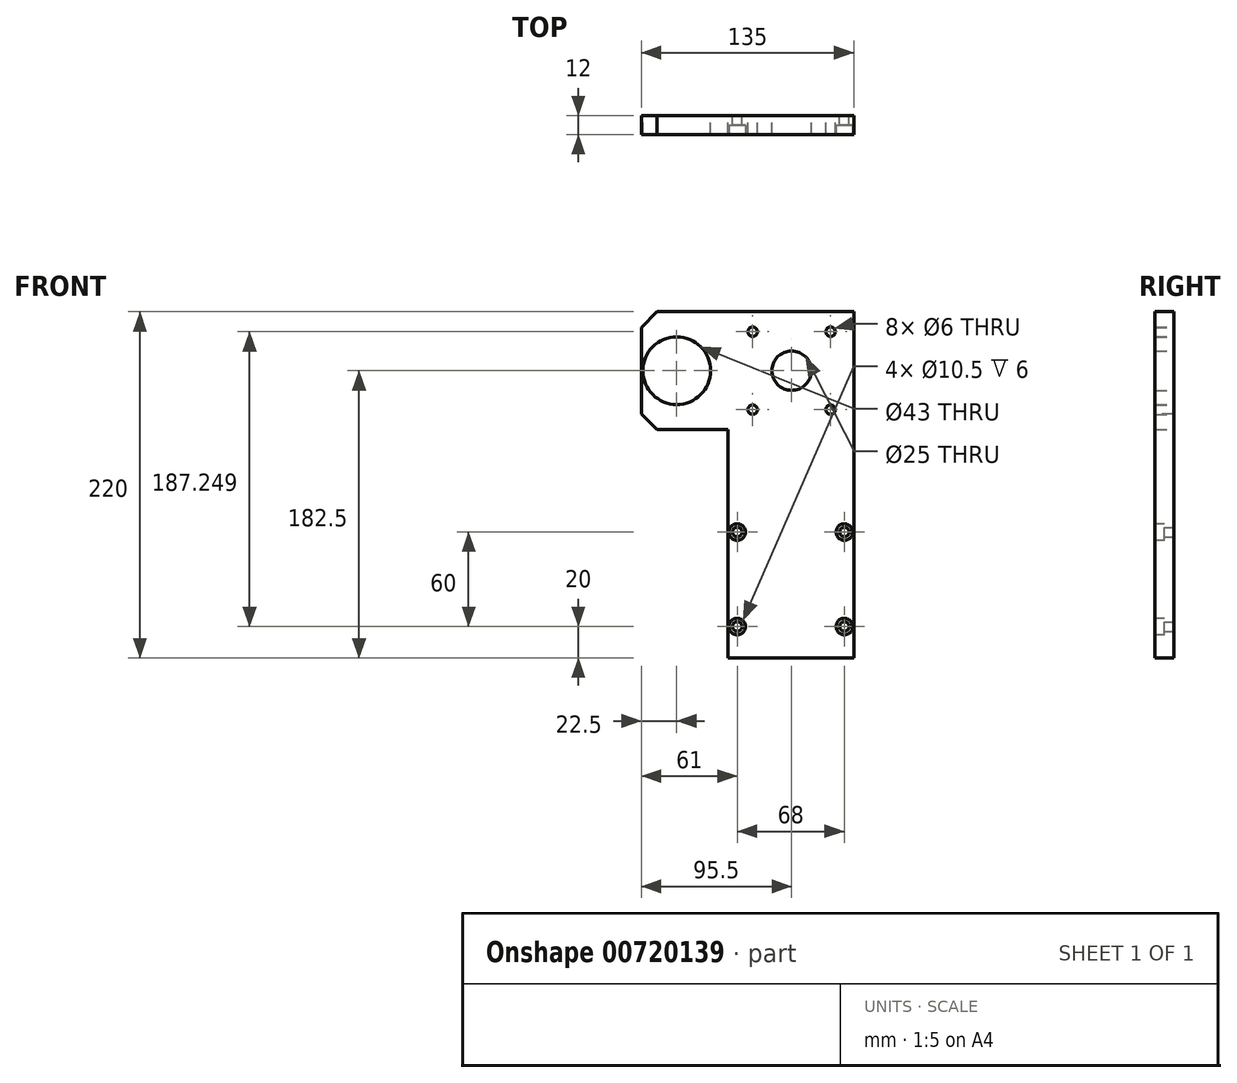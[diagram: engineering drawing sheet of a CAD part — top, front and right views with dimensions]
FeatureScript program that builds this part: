
annotation { "Feature Type Name" : "Feature", "Feature Type Description" : "" }
export const myFeature = defineFeature(function(context is Context, id is Id, definition is map)
    precondition{}
    {
        {
            var Q0;
            Q0=qCreatedBy(makeId("Front.planeOp"),FACE);
            var sketch = newSketch(context, id + "F0", { "sketchPlane" : qUnion([Q0])});
            skLineSegment(sketch, "E0", {"start": v(0, 0) * mm, "end": v(80, 0) * mm});
            skLineSegment(sketch, "E1", {"start": v(80, 0) * mm, "end": v(80, 220) * mm});
            skLineSegment(sketch, "E2", {"start": v(80, 220) * mm, "end": v(-55, 220) * mm});
            skLineSegment(sketch, "E3", {"start": v(-55, 220) * mm, "end": v(-55, 145) * mm});
            skLineSegment(sketch, "E4", {"start": v(-55, 145) * mm, "end": v(0, 145) * mm});
            skLineSegment(sketch, "E5", {"start": v(0, 145) * mm, "end": v(0, 0) * mm});
            skCircle(sketch, "E6", {"center": v(-32.5, 182.5) * mm, "radius": 21.5 * mm});
            skPoint(sketch, "E6.centerSnap0", {"position": v(-55, 182.5) * mm});
            skCircle(sketch, "E7", {"center": v(6, 20) * mm, "radius": 3 * mm});
            skCircle(sketch, "E8", {"center": v(6, 80) * mm, "radius": 3 * mm});
            skCircle(sketch, "E9", {"center": v(74, 80) * mm, "radius": 3 * mm});
            skCircle(sketch, "E10", {"center": v(74, 20) * mm, "radius": 3 * mm});
            skCircle(sketch, "E11", {"center": v(40.5, 182.5) * mm, "radius": 12.5 * mm});
            skCircle(sketch, "E12", {"center": v(40.5, 182.5) * mm, "radius": 35 * mm, "construction": true});
            skLineSegment(sketch, "E13", {"start": v(40.5, 182.5) * mm, "end": v(15.75, 207.25) * mm, "construction": true});
            skCircle(sketch, "E14", {"center": v(15.75, 207.25) * mm, "radius": 3 * mm});
            skCircle(sketch, "E15", {"center": v(65.25, 207.25) * mm, "radius": 3 * mm});
            skCircle(sketch, "E16", {"center": v(15.75, 157.75) * mm, "radius": 3 * mm});
            skCircle(sketch, "E17", {"center": v(65.25, 157.75) * mm, "radius": 3 * mm});
            skSolve(sketch);
        }
        {
            var Q0;
            Q0=makeQuery(id+"F0.imprint","IMPRINT",FACE,{"disambiguationData":[TD([[makeQuery(id+"F0.imprint","IMPRINT",EDGE,{"derivedFrom":sQuery(id+"F0.wireOp",EDGE,"E0")}),1.0]])]});
            extrude(context, id + "F1", {"entities" : qUnion([Q0]), "depth" : 12 * mm, "offsetDistance" : 25 * mm});
        }
        {
            var Q0;
            Q0=makeQuery(id+"F1.opExtrude","SWEPT_EDGE",EDGE,{"disambiguationData":[OSD([sQuery(id+"F0.wireOp",EDGE,"E2"),sQuery(id+"F0.wireOp",EDGE,"E3")])]});
            var Q1;
            Q1=makeQuery(id+"F1.opExtrude","SWEPT_EDGE",EDGE,{"disambiguationData":[OSD([sQuery(id+"F0.wireOp",EDGE,"E3"),sQuery(id+"F0.wireOp",EDGE,"E4")])]});
            chamfer(context, id + "F2", {"entities" : qUnion([Q0, Q1]), "width" : 10 * mm, "tangentPropagation" : true});
        }
        {
            var Q0;
            Q0=makeQuery(id+"F1.opExtrude","CAP_FACE",FACE,{"disambiguationData":[OSD([sQuery(id+"F0.wireOp",EDGE,"E0"),sQuery(id+"F0.wireOp",EDGE,"E1"),sQuery(id+"F0.wireOp",EDGE,"E2"),sQuery(id+"F0.wireOp",EDGE,"E3"),sQuery(id+"F0.wireOp",EDGE,"E4"),sQuery(id+"F0.wireOp",EDGE,"E5"),sQuery(id+"F0.wireOp",EDGE,"E6"),sQuery(id+"F0.wireOp",EDGE,"E7"),sQuery(id+"F0.wireOp",EDGE,"E8"),sQuery(id+"F0.wireOp",EDGE,"E9"),sQuery(id+"F0.wireOp",EDGE,"E10"),sQuery(id+"F0.wireOp",EDGE,"E11"),sQuery(id+"F0.wireOp",EDGE,"E14"),sQuery(id+"F0.wireOp",EDGE,"E15"),sQuery(id+"F0.wireOp",EDGE,"E16"),sQuery(id+"F0.wireOp",EDGE,"E17")])],"isStart":false});
            var sketch = newSketch(context, id + "F3", { "sketchPlane" : qUnion([Q0])});
            skCircle(sketch, "E18", {"center": v(6, 80) * mm, "radius": 5.25 * mm});
            skCircle(sketch, "E19", {"center": v(74, 80) * mm, "radius": 5.25 * mm});
            skCircle(sketch, "E20", {"center": v(74, 20) * mm, "radius": 5.25 * mm});
            skCircle(sketch, "E21", {"center": v(6, 20) * mm, "radius": 5.25 * mm});
            skSolve(sketch);
        }
        {
            var Q0;
            Q0=makeQuery(id+"F3.imprint","IMPRINT",FACE,{"disambiguationData":[TD([[makeQuery(id+"F3.imprint","IMPRINT",EDGE,{"derivedFrom":sQuery(id+"F3.wireOp",EDGE,"E18")}),1.0]])]});
            var Q1;
            Q1=makeQuery(id+"F3.imprint","IMPRINT",FACE,{"disambiguationData":[TD([[makeQuery(id+"F3.imprint","IMPRINT",EDGE,{"derivedFrom":sQuery(id+"F3.wireOp",EDGE,"E19")}),1.0]])]});
            var Q2;
            Q2=makeQuery(id+"F3.imprint","IMPRINT",FACE,{"disambiguationData":[TD([[makeQuery(id+"F3.imprint","IMPRINT",EDGE,{"derivedFrom":sQuery(id+"F3.wireOp",EDGE,"E20")}),1.0]])]});
            var Q3;
            Q3=makeQuery(id+"F3.imprint","IMPRINT",FACE,{"disambiguationData":[TD([[makeQuery(id+"F3.imprint","IMPRINT",EDGE,{"derivedFrom":sQuery(id+"F3.wireOp",EDGE,"E21")}),1.0]])]});
            extrude(context, id + "F4", {"entities" : qUnion([Q0, Q1, Q2, Q3]), "operationType" : NewBodyOperationType.REMOVE, "oppositeDirection" : true, "depth" : 6 * mm, "offsetDistance" : 25 * mm});
        }
    });
